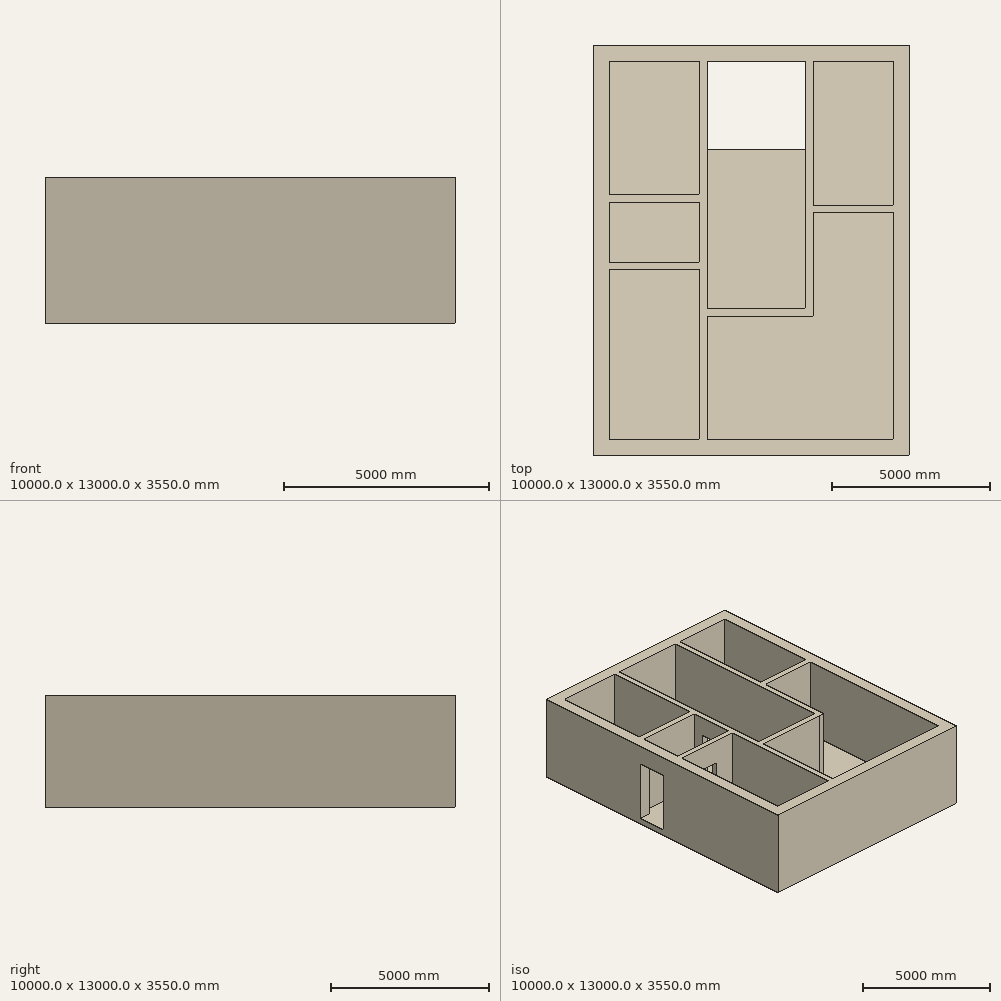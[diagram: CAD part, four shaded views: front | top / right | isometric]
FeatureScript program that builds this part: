
annotation { "Feature Type Name" : "Feature", "Feature Type Description" : "" }
export const myFeature = defineFeature(function(context is Context, id is Id, definition is map)
    precondition{}
    {
        {
            var Q0;
            Q0=qCreatedBy(makeId("Top.planeOp"),FACE);
            var sketch = newSketch(context, id + "F0", { "sketchPlane" : qUnion([Q0])});
            skLineSegment(sketch, "E0.bottom", {"start": v(5000, 6500) * mm, "end": v(-5000, 6500) * mm});
            skLineSegment(sketch, "E0.top", {"start": v(5000, -6500) * mm, "end": v(-5000, -6500) * mm});
            skLineSegment(sketch, "E0.left", {"start": v(5000, 6500) * mm, "end": v(5000, -6500) * mm});
            skLineSegment(sketch, "E0.right", {"start": v(-5000, 6500) * mm, "end": v(-5000, -6500) * mm});
            skPoint(sketch, "E0.middle", {"position": v(0, 0) * mm});
            skSolve(sketch);
        }
        {
            var Q0;
            Q0 = qSketchRegion(id + "F0", true);
            extrude(context, id + "F1", {"entities" : qUnion([Q0]), "depth" : 3550 * mm, "offsetDistance" : 25 * mm});
        }
        {
            var Q0;
            Q0=makeQuery(id+"F1.opExtrude","CAP_FACE",FACE,{"disambiguationData":[OSD([sQuery(id+"F0.wireOp",EDGE,"E0.bottom"),sQuery(id+"F0.wireOp",EDGE,"E0.top"),sQuery(id+"F0.wireOp",EDGE,"E0.left"),sQuery(id+"F0.wireOp",EDGE,"E0.right")])],"isStart":false});
            var sketch = newSketch(context, id + "F2", { "sketchPlane" : qUnion([Q0])});
            skLineSegment(sketch, "E1.0", {"start": v(-4500, 6000) * mm, "end": v(-4500, -6000) * mm});
            skLineSegment(sketch, "E1.1", {"start": v(4500, 6000) * mm, "end": v(-4500, 6000) * mm});
            skLineSegment(sketch, "E1.2", {"start": v(4500, 6000) * mm, "end": v(4500, -6000) * mm});
            skLineSegment(sketch, "E1.3", {"start": v(4500, -6000) * mm, "end": v(-4500, -6000) * mm});
            skSolve(sketch);
        }
        {
            var Q0;
            Q0 = qSketchRegion(id + "F2", true);
            var Q1;
            Q1=makeQuery(id+"F2.imprint","IMPRINT",FACE,{"disambiguationData":[TD([[makeQuery(id+"F2.imprint","IMPRINT",EDGE,{"derivedFrom":sQuery(id+"F2.wireOp",EDGE,"6241154e-0bf6-49ba-bd71-02362f76f25d.0")}),1.0]])]});
            extrude(context, id + "F3", {"entities" : qUnion([Q0, Q1]), "operationType" : NewBodyOperationType.REMOVE, "oppositeDirection" : true, "depth" : 3300 * mm, "offsetDistance" : 25 * mm});
        }
        {
            var Q0;
            Q0=makeQuery(id+"F3.boolean.opBoolean","COPY",FACE,{"derivedFrom":makeQuery(id+"F3.opExtrude","CAP_FACE",FACE,{"disambiguationData":[OSD([sQuery(id+"F2.wireOp",EDGE,"E1.0"),sQuery(id+"F2.wireOp",EDGE,"E1.1"),sQuery(id+"F2.wireOp",EDGE,"E1.2"),sQuery(id+"F2.wireOp",EDGE,"E1.3")])],"isStart":false})});
            var sketch = newSketch(context, id + "F4", { "sketchPlane" : qUnion([Q0])});
            skLineSegment(sketch, "E2", {"start": v(-4500, -366.62) * mm, "end": v(-1660.5, -366.62) * mm});
            skLineSegment(sketch, "E3", {"start": v(-1660.5, -616.62) * mm, "end": v(-1660.5, -6000) * mm});
            skLineSegment(sketch, "E4", {"start": v(-1660.5, -366.62) * mm, "end": v(-1660.5, 1531.45) * mm});
            skLineSegment(sketch, "E5", {"start": v(-1660.5, 1531.45) * mm, "end": v(-4500, 1531.45) * mm});
            skLineSegment(sketch, "E6", {"start": v(-4500, 1531.45) * mm, "end": v(-1660.5, 1531.45) * mm});
            skLineSegment(sketch, "E7", {"start": v(-1660.5, 1781.45) * mm, "end": v(-1660.5, 6000) * mm});
            skLineSegment(sketch, "E8", {"start": v(1725.2, 1441.9) * mm, "end": v(1725.2, 6000) * mm});
            skLineSegment(sketch, "E9", {"start": v(1975.2, 1441.9) * mm, "end": v(4500, 1441.9) * mm});
            skLineSegment(sketch, "E10", {"start": v(1725.2, 1441.9) * mm, "end": v(1725.2, -1827.54) * mm});
            skLineSegment(sketch, "E11", {"start": v(-1410.5, -2077.54) * mm, "end": v(1725.2, -2077.54) * mm});
            skLineSegment(sketch, "E12.0", {"start": v(-4500, -616.62) * mm, "end": v(-1660.5, -616.62) * mm});
            skLineSegment(sketch, "E13.0", {"start": v(-1410.5, 6000) * mm, "end": v(-1410.5, -1827.54) * mm});
            skLineSegment(sketch, "E14.0", {"start": v(-4500, 1781.45) * mm, "end": v(-1660.5, 1781.45) * mm});
            skLineSegment(sketch, "E15.0", {"start": v(-1410.5, -1827.54) * mm, "end": v(1725.2, -1827.54) * mm});
            skLineSegment(sketch, "E16.trimOffspring", {"start": v(-1410.5, -2077.54) * mm, "end": v(-1410.5, -6000) * mm});
            skLineSegment(sketch, "E17.0", {"start": v(1975.2, 1441.9) * mm, "end": v(1975.2, 6000) * mm});
            skLineSegment(sketch, "E18.0", {"start": v(1975.19, 1191.9) * mm, "end": v(4500, 1191.9) * mm});
            skLineSegment(sketch, "E19.0", {"start": v(1975.19, 1191.9) * mm, "end": v(1975.13, -2083.27) * mm});
            skLineSegment(sketch, "E20", {"start": v(1975.13, -2083.27) * mm, "end": v(1725.2, -2077.54) * mm});
            skLineSegment(sketch, "E21", {"start": v(4500, 1191.9) * mm, "end": v(4500, 1441.9) * mm});
            skLineSegment(sketch, "E22", {"start": v(1975.2, 6000) * mm, "end": v(1725.2, 6000) * mm});
            skLineSegment(sketch, "E23", {"start": v(-1410.5, 6000) * mm, "end": v(-1660.5, 6000) * mm});
            skLineSegment(sketch, "E24", {"start": v(-4500, 1781.45) * mm, "end": v(-4500, 1531.45) * mm});
            skLineSegment(sketch, "E25", {"start": v(-4500, -366.62) * mm, "end": v(-4500, -616.62) * mm});
            skLineSegment(sketch, "E26", {"start": v(-1660.5, -6000) * mm, "end": v(-1410.5, -6000) * mm});
            skSolve(sketch);
        }
        {
            var Q0;
            Q0=makeQuery(id+"F4.imprint","IMPRINT",FACE,{"disambiguationData":[TD([[makeQuery(id+"F4.imprint","IMPRINT",EDGE,{"derivedFrom":sQuery(id+"F4.wireOp",EDGE,"E2")}),-1.0]])]});
            extrude(context, id + "F5", {"entities" : qUnion([Q0]), "operationType" : NewBodyOperationType.ADD, "depth" : 3300 * mm, "offsetDistance" : 25 * mm});
        }
        {
            var Q0;
            Q0=makeQuery(id+"F5.opExtrude","SWEPT_FACE",FACE,{"disambiguationData":[OSD([sQuery(id+"F4.wireOp",EDGE,"E12.0")])]});
            var sketch = newSketch(context, id + "F6", { "sketchPlane" : qUnion([Q0])});
            skLineSegment(sketch, "E27.bottom", {"start": v(-3580.25, 250) * mm, "end": v(-2580.25, 250) * mm});
            skLineSegment(sketch, "E27.top", {"start": v(-3580.25, 2550) * mm, "end": v(-2580.25, 2550) * mm});
            skLineSegment(sketch, "E27.left", {"start": v(-3580.25, 250) * mm, "end": v(-3580.25, 2550) * mm});
            skLineSegment(sketch, "E27.right", {"start": v(-2580.25, 250) * mm, "end": v(-2580.25, 2550) * mm});
            skLineSegment(sketch, "E28", {"start": v(-3580.25, 2550) * mm, "end": v(-4500, 2550) * mm, "construction": true});
            skLineSegment(sketch, "E29", {"start": v(-2580.25, 2550) * mm, "end": v(-1660.5, 2550) * mm, "construction": true});
            skSolve(sketch);
        }
        {
            var Q0;
            Q0=makeQuery(id+"F6.imprint","IMPRINT",FACE,{"disambiguationData":[TD([[makeQuery(id+"F6.imprint","IMPRINT",EDGE,{"derivedFrom":sQuery(id+"F6.wireOp",EDGE,"E27.bottom")}),1.0]])]});
            extrude(context, id + "F7", {"entities" : qUnion([Q0]), "operationType" : NewBodyOperationType.REMOVE, "oppositeDirection" : true, "depth" : 250 * mm, "offsetDistance" : 25 * mm});
        }
        {
            var Q0;
            {var subQ1=sQuery(id+"F4.wireOp",EDGE,"E2");var subQ2=sQuery(id+"F2.wireOp",EDGE,"E1.0");Q0=makeQuery(id+"F5.boolean.opBoolean","SPLIT",FACE,{"disambiguationData":[TD([makeQuery(id+"F5.opExtrude","SWEPT_FACE",FACE,{"disambiguationData":[OSD([subQ1])]})])],"derivedFrom":makeQuery(id+"F3.boolean.opBoolean","COPY",FACE,{"derivedFrom":makeQuery(id+"F3.opExtrude","SWEPT_FACE",FACE,{"disambiguationData":[OSD([subQ2])]})})});}
            var sketch = newSketch(context, id + "F8", { "sketchPlane" : qUnion([Q0])});
            skLineSegment(sketch, "E30.bottom", {"start": v(1232.41, 250) * mm, "end": v(-67.59, 250) * mm});
            skLineSegment(sketch, "E30.top", {"start": v(1232.41, 2750) * mm, "end": v(-67.59, 2750) * mm});
            skLineSegment(sketch, "E30.left", {"start": v(1232.41, 250) * mm, "end": v(1232.41, 2750) * mm});
            skLineSegment(sketch, "E30.right", {"start": v(-67.59, 250) * mm, "end": v(-67.59, 2750) * mm});
            skLineSegment(sketch, "E31", {"start": v(1232.41, 2750) * mm, "end": v(1531.45, 2750) * mm, "construction": true});
            skLineSegment(sketch, "E32", {"start": v(-67.59, 2750) * mm, "end": v(-366.62, 2750) * mm, "construction": true});
            skSolve(sketch);
        }
        {
            var Q0;
            Q0 = qSketchRegion(id + "F8", true);
            var Q1;
            Q1=makeQuery(id+"FDxpAjxFoEipkFc_1.boolean.opBoolean","MERGE",FACE,{"derivedFrom":[makeQuery(id+"F1.opExtrude","SWEPT_FACE",FACE,{"disambiguationData":[OSD([sQuery(id+"F0.wireOp",EDGE,"E0.right")])]}),makeQuery(id+"FDxpAjxFoEipkFc_1.opExtrude","SWEPT_FACE",FACE,{"disambiguationData":[OSD([sQuery(id+"FfuZhybFKGmWld3_1.wireOp",EDGE,"d30b5233-8d14-4786-95f0-92fd1949041e.0.1")])]})]});
            extrude(context, id + "F9", {"entities" : qUnion([Q0]), "operationType" : NewBodyOperationType.REMOVE, "endBound" : BoundingType.UP_TO_SURFACE, "oppositeDirection" : true, "depth" : 25 * mm, "endBoundEntityFace" : qUnion([Q1]), "offsetDistance" : 25 * mm});
        }
        {
            var Q0;
            Q0=makeQuery(id+"F5.opExtrude","SWEPT_FACE",FACE,{"disambiguationData":[OSD([sQuery(id+"F4.wireOp",EDGE,"E4")])]});
            var sketch = newSketch(context, id + "F10", { "sketchPlane" : qUnion([Q0])});
            skLineSegment(sketch, "E33.bottom", {"start": v(-82.41, 250) * mm, "end": v(-1082.41, 250) * mm});
            skLineSegment(sketch, "E33.top", {"start": v(-82.41, 2750) * mm, "end": v(-1082.41, 2750) * mm});
            skLineSegment(sketch, "E33.left", {"start": v(-82.41, 250) * mm, "end": v(-82.41, 2750) * mm});
            skLineSegment(sketch, "E33.right", {"start": v(-1082.41, 250) * mm, "end": v(-1082.41, 2750) * mm});
            skLineSegment(sketch, "E34", {"start": v(-1082.41, 2750) * mm, "end": v(-1531.45, 2750) * mm, "construction": true});
            skLineSegment(sketch, "E35", {"start": v(-82.41, 2750) * mm, "end": v(366.62, 2750) * mm, "construction": true});
            skSolve(sketch);
        }
        {
            var Q0;
            Q0 = qSketchRegion(id + "F10", true);
            var Q1;
            Q1=makeQuery(id+"F5.opExtrude","SWEPT_FACE",FACE,{"disambiguationData":[OSD([sQuery(id+"F4.wireOp",EDGE,"E13.0")])]});
            extrude(context, id + "F11", {"entities" : qUnion([Q0]), "operationType" : NewBodyOperationType.REMOVE, "endBound" : BoundingType.UP_TO_SURFACE, "oppositeDirection" : true, "depth" : 25 * mm, "endBoundEntityFace" : qUnion([Q1]), "offsetDistance" : 25 * mm});
        }
        {
            var Q0;
            {var subQ0=sQuery(id+"F2.wireOp",EDGE,"E1.0");var subQ2=sQuery(id+"F2.wireOp",EDGE,"E1.3");var subQ3=sQuery(id+"F2.wireOp",EDGE,"E1.1");var subQ4=makeQuery(id+"F3.boolean.opBoolean","COPY",FACE,{"derivedFrom":makeQuery(id+"F3.opExtrude","CAP_FACE",FACE,{"disambiguationData":[OSD([subQ0,subQ3,sQuery(id+"F2.wireOp",EDGE,"E1.2"),subQ2])],"isStart":false})});Q0=makeQuery(id+"F11.boolean.opBoolean","MERGE",FACE,{"derivedFrom":[makeQuery(id+"F5.boolean.opBoolean","SPLIT",FACE,{"disambiguationData":[TD([makeQuery(id+"F5.opExtrude","SWEPT_FACE",FACE,{"disambiguationData":[OSD([sQuery(id+"F4.wireOp",EDGE,"E13.0")])]})])],"derivedFrom":subQ4}),makeQuery(id+"F9.boolean.opBoolean","MERGE",FACE,{"derivedFrom":[makeQuery(id+"F7.boolean.opBoolean","MERGE",FACE,{"derivedFrom":[makeQuery(id+"F5.boolean.opBoolean","SPLIT",FACE,{"disambiguationData":[TD([makeQuery(id+"F5.opExtrude","SWEPT_FACE",FACE,{"disambiguationData":[OSD([sQuery(id+"F4.wireOp",EDGE,"E2")])]})])],"derivedFrom":subQ4}),makeQuery(id+"F5.boolean.opBoolean","SPLIT",FACE,{"disambiguationData":[TD([makeQuery(id+"F5.opExtrude","SWEPT_FACE",FACE,{"disambiguationData":[OSD([sQuery(id+"F4.wireOp",EDGE,"E3")])]})])],"derivedFrom":subQ4}),makeQuery(id+"F7.opExtrude","SWEPT_FACE",FACE,{"disambiguationData":[OSD([sQuery(id+"F6.wireOp",EDGE,"E27.bottom")])]})]}),makeQuery(id+"F9.opExtrude","SWEPT_FACE",FACE,{"disambiguationData":[OSD([sQuery(id+"F8.wireOp",EDGE,"E30.bottom")])]})]}),makeQuery(id+"F11.opExtrude","SWEPT_FACE",FACE,{"disambiguationData":[OSD([sQuery(id+"F10.wireOp",EDGE,"E33.bottom")])]})]});}
            var sketch = newSketch(context, id + "F12", { "sketchPlane" : qUnion([Q0])});
            skLineSegment(sketch, "E36.bottom", {"start": v(-1410.5, 3200) * mm, "end": v(1725.2, 3200) * mm});
            skLineSegment(sketch, "E36.top", {"start": v(-1410.5, 6000) * mm, "end": v(1725.2, 6000) * mm});
            skLineSegment(sketch, "E36.left", {"start": v(-1410.5, 3200) * mm, "end": v(-1410.5, 6000) * mm});
            skLineSegment(sketch, "E36.right", {"start": v(1725.2, 3200) * mm, "end": v(1725.2, 6000) * mm});
            skSolve(sketch);
        }
        {
            var Q0;
            Q0=makeQuery(id+"F12.imprint","IMPRINT",FACE,{"disambiguationData":[TD([[makeQuery(id+"F12.imprint","IMPRINT",EDGE,{"derivedFrom":sQuery(id+"F12.wireOp",EDGE,"E36.bottom")}),1.0]])]});
            extrude(context, id + "F13", {"entities" : qUnion([Q0]), "operationType" : NewBodyOperationType.REMOVE, "endBound" : BoundingType.UP_TO_NEXT, "oppositeDirection" : true, "depth" : 25 * mm, "offsetDistance" : 25 * mm});
        }
    });
